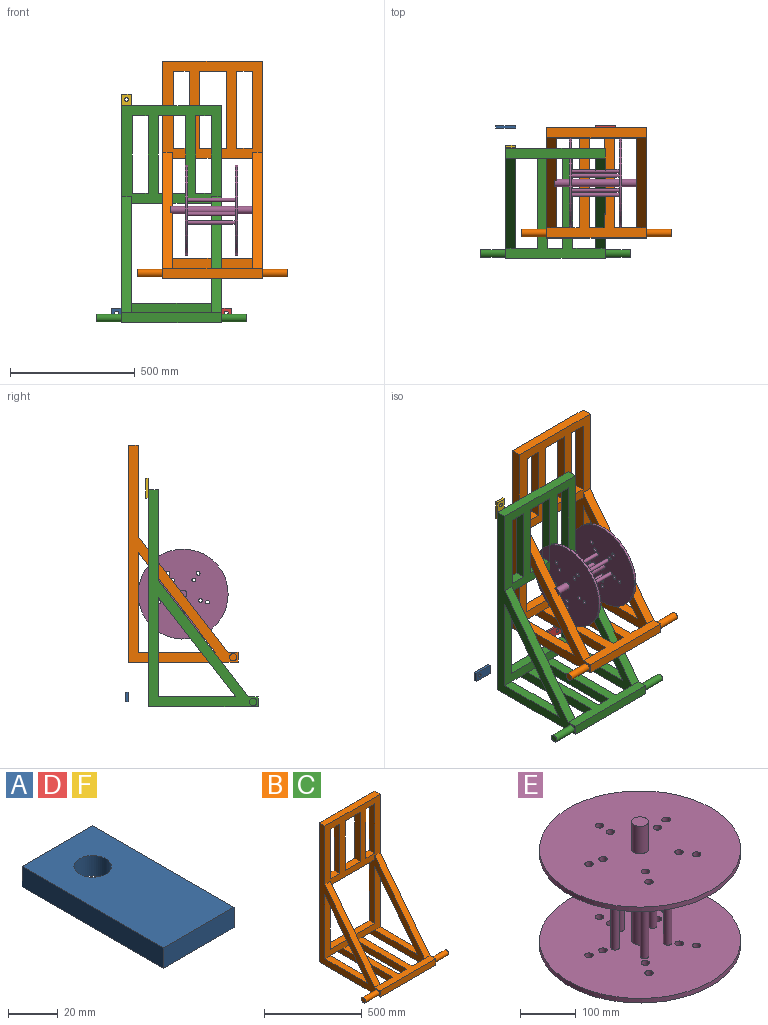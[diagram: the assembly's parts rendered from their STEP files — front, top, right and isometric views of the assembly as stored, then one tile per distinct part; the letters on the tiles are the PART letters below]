
ASSEMBLY  parts=6 mates=3
PART A: 7 faces, bbox 40x80x10 mm
  f0: plane 40x10mm, normal (0,1,0), area 400mm2, adj f1,f4,f5,f6
  f1: plane 80x10mm, normal (-1,0,0), area 800mm2, adj f0,f2,f5,f6
  f2: plane 40x10mm, normal (0,-1,0), area 400mm2, adj f1,f4,f5,f6
  f3: cylinder r=7.5mm len=15mm, axis (0,0,-1), area 471.2mm2, adj f5,f6
  f4: plane 80x10mm, normal (1,0,0), area 800mm2, adj f0,f2,f5,f6
  f5: plane 80x40mm, normal (0,0,1), area 3023.3mm2, adj f0,f1,f2,f3,f4
  f6: plane 80x40mm, normal (0,0,-1), area 3023.3mm2, adj f0,f1,f2,f3,f4
PART B: 45 faces, bbox 600x440x870 mm
  f0: plane 400x390mm, normal (0,-1,0), area 80507.1mm2, adj f5,f6,f7,f8,f9,f10,f11,f12
  f1: plane 400x400mm, normal (0,0,1), area 44800mm2, adj f8,f19,f24,f28,f29,f30,f31,f34
  f2: plane 90x40mm, normal (0,0,-1), area 3600mm2, adj f17,f24,f25,f30
  f3: plane 60x40mm, normal (0,0,-1), area 2400mm2, adj f24,f25,f29,f31
  f4: plane 90x40mm, normal (0,0,-1), area 3600mm2, adj f22,f24,f25,f28
  f5: plane 310x40mm, normal (-1,0,0), area 12400mm2, adj f0,f6,f23,f25
  f6: plane 109.75x40mm, normal (0,0,1), area 4390mm2, adj f0,f5,f7,f25
  f7: plane 310x40mm, normal (1,0,0), area 12400mm2, adj f0,f6,f23,f25
  f8: plane 870x440mm, normal (1,0,0), area 71974.7mm2, adj f0,f1,f9,f24,f25,f26,f27,f38
  f9: plane 400x40mm, normal (0,0,1), area 16000mm2, adj f0,f8,f19,f25
  f10: plane 63.61x40mm, normal (0,0,1), area 2544.6mm2, adj f0,f11,f20,f25
  f11: plane 310x40mm, normal (1,0,0), area 12400mm2, adj f0,f10,f12,f25
  f12: plane 63.61x40mm, normal (0,0,-1), area 2544.6mm2, adj f0,f11,f20,f25
  f13: plane 63.61x40mm, normal (0,0,1), area 2544.6mm2, adj f0,f14,f21,f25
  f14: plane 310x40mm, normal (1,0,0), area 12400mm2, adj f0,f13,f15,f25
  f15: plane 63.61x40mm, normal (0,0,-1), area 2544.6mm2, adj f0,f14,f21,f25
  f16: plane 320x40mm, normal (0,0,1), area 12800mm2, adj f17,f22,f24,f25
  f17: plane 505.37x400mm, normal (1,0,0), area 53881.6mm2, adj f0,f2,f16,f18,f24,f25,f27,f32
  f18: plane 320x40mm, normal (0,0,-1), area 12800mm2, adj f0,f17,f22,f25
  f19: plane 870x440mm, normal (-1,0,0), area 71974.7mm2, adj f0,f1,f9,f24,f25,f27,f32,f33
  f20: plane 310x40mm, normal (-1,0,0), area 12400mm2, adj f0,f10,f12,f25
  f21: plane 310x40mm, normal (-1,0,0), area 12400mm2, adj f0,f13,f15,f25
  f22: plane 505.37x400mm, normal (-1,0,0), area 53881.6mm2, adj f0,f4,f16,f18,f24,f25,f26,f27
  f23: plane 109.75x40mm, normal (0,0,-1), area 4390mm2, adj f0,f5,f7,f25
  f24: plane 400x400mm, normal (0,-1,0), area 44800mm2, adj f1,f2,f3,f4,f8,f16,f17,f19
  f25: plane 870x400mm, normal (0,1,0), area 136937mm2, adj f2,f3,f4,f5,f6,f7,f8,f9
  f26: plane 309.43x40mm, normal (0,0,1), area 12377.1mm2, adj f8,f22,f24,f40
  f27: plane 440x400mm, normal (0,0,-1), area 80000mm2, adj f8,f17,f19,f22,f25,f28,f29,f30
  f28: plane 400x40mm, normal (1,0,0), area 16000mm2, adj f1,f4,f25,f27,f35
  f29: plane 400x40mm, normal (-1,0,0), area 16000mm2, adj f1,f3,f25,f27,f36
  f30: plane 400x40mm, normal (-1,0,0), area 16000mm2, adj f1,f2,f25,f27,f37
  f31: plane 400x40mm, normal (1,0,0), area 16000mm2, adj f1,f3,f25,f27,f36
  f32: plane 309.43x40mm, normal (0,0,1), area 12377.1mm2, adj f17,f19,f24,f33
  f33: plane 400x309.43mm, normal (0,0.79,-0.61), area 20228.5mm2, adj f17,f19,f24,f32
  f34: plane 465.37x360mm, normal (0,-0.79,0.61), area 23534.6mm2, adj f0,f1,f17,f19
  f35: plane 90x40mm, normal (0,1,0), area 3600mm2, adj f1,f22,f27,f28
  f36: plane 60x40mm, normal (0,1,0), area 2400mm2, adj f1,f27,f29,f31
  f37: plane 90x40mm, normal (0,1,0), area 3600mm2, adj f1,f17,f27,f30
  f38: plane 400x40mm, normal (0,-1,0), area 16000mm2, adj f1,f8,f19,f27
  f39: plane 465.37x360mm, normal (0,-0.79,0.61), area 23534.6mm2, adj f0,f1,f8,f22
  f40: plane 400x309.43mm, normal (0,0.79,-0.61), area 20228.5mm2, adj f8,f22,f24,f26
  f41: cylinder r=15mm len=100mm, axis (-1,0,0), area 9424.8mm2, adj f8,f42
  f42: plane 30x30mm, normal (1,0,0), area 706.9mm2, adj f41
  f43: cylinder r=15mm len=100mm, axis (1,0,0), area 9424.8mm2, adj f19,f44
  f44: plane 30x30mm, normal (-1,0,0), area 706.9mm2, adj f43
PART C: same geometry as B
PART D: same geometry as A
PART E: 36 faces, bbox 360x360x330 mm
  f0: cylinder r=180mm len=360mm, axis (0,0,-1), area 11309.7mm2, adj f1,f2
  f1: plane 360x360mm, normal (0,0,1), area 98430mm2, adj f0,f3,f4,f5,f6,f7,f8,f26
  f2: plane 360x360mm, normal (0,0,-1), area 99313.6mm2, adj f0,f12,f26,f27,f28,f29,f30,f31
  f3: cylinder r=15mm len=190mm, axis (0,0,-1), area 17907.1mm2, adj f1,f11
  f4: cylinder r=7.5mm len=190mm, axis (0,0,-1), area 8953.5mm2, adj f1,f11
  f5: cylinder r=7.5mm len=190mm, axis (0,0,-1), area 8953.5mm2, adj f1,f11
  f6: cylinder r=7.5mm len=190mm, axis (0,0,-1), area 8953.5mm2, adj f1,f11
  f7: cylinder r=7.5mm len=190mm, axis (0,0,-1), area 8953.5mm2, adj f1,f11
  f8: cylinder r=7.5mm len=190mm, axis (0,0,-1), area 8953.5mm2, adj f1,f11
  f9: cylinder r=180mm len=360mm, axis (0,0,-1), area 11309.7mm2, adj f10,f11
  f10: plane 360x360mm, normal (0,0,1), area 99313.6mm2, adj f9,f14,f16,f17,f18,f19,f20,f21
  f11: plane 360x360mm, normal (0,0,-1), area 98430mm2, adj f3,f4,f5,f6,f7,f8,f9,f16
  f12: cylinder r=15mm len=60mm, axis (0,0,1), area 5654.9mm2, adj f2,f13
  f13: plane 30x30mm, normal (0,0,-1), area 706.9mm2, adj f12
  f14: cylinder r=15mm len=60mm, axis (0,0,-1), area 5654.9mm2, adj f10,f15
  f15: plane 30x30mm, normal (0,0,1), area 706.9mm2, adj f14
  f16: cylinder r=7.5mm len=15mm, axis (0,0,-1), area 471.2mm2, adj f10,f11
  f17: cylinder r=7.5mm len=15mm, axis (0,0,-1), area 471.2mm2, adj f10,f11
  f18: cylinder r=7.5mm len=15mm, axis (0,0,-1), area 471.2mm2, adj f10,f11
  f19: cylinder r=7.5mm len=15mm, axis (0,0,-1), area 471.2mm2, adj f10,f11
  f20: cylinder r=7.5mm len=15mm, axis (0,0,-1), area 471.2mm2, adj f10,f11
  f21: cylinder r=7.5mm len=15mm, axis (0,0,-1), area 471.2mm2, adj f10,f11
  f22: cylinder r=7.5mm len=15mm, axis (0,0,-1), area 471.2mm2, adj f10,f11
  f23: cylinder r=7.5mm len=15mm, axis (0,0,-1), area 471.2mm2, adj f10,f11
  f24: cylinder r=7.5mm len=15mm, axis (0,0,-1), area 471.2mm2, adj f10,f11
  f25: cylinder r=7.5mm len=15mm, axis (0,0,-1), area 471.2mm2, adj f10,f11
  f26: cylinder r=7.5mm len=15mm, axis (0,0,-1), area 471.2mm2, adj f1,f2
  f27: cylinder r=7.5mm len=15mm, axis (0,0,-1), area 471.2mm2, adj f1,f2
  f28: cylinder r=7.5mm len=15mm, axis (0,0,-1), area 471.2mm2, adj f1,f2
  f29: cylinder r=7.5mm len=15mm, axis (0,0,-1), area 471.2mm2, adj f1,f2
  f30: cylinder r=7.5mm len=15mm, axis (0,0,-1), area 471.2mm2, adj f1,f2
  f31: cylinder r=7.5mm len=15mm, axis (0,0,-1), area 471.2mm2, adj f1,f2
  f32: cylinder r=7.5mm len=15mm, axis (0,0,-1), area 471.2mm2, adj f1,f2
  f33: cylinder r=7.5mm len=15mm, axis (0,0,-1), area 471.2mm2, adj f1,f2
  f34: cylinder r=7.5mm len=15mm, axis (0,0,-1), area 471.2mm2, adj f1,f2
  f35: cylinder r=7.5mm len=15mm, axis (0,0,-1), area 471.2mm2, adj f1,f2
PART F: same geometry as A
PLACE A rot(axis=(-0.58,0.58,0.58),120deg) t=(-227.2,31.63,-720.68)mm
PLACE B t=(-102.52,31.63,268.85)mm
PLACE C t=(-267.2,-49.25,89.32)mm
PLACE D rot(axis=(-0.58,-0.58,-0.58),120deg) t=(92.8,31.63,-760.68)mm
PLACE E rot(axis=(-0.58,0.58,-0.58),120deg) t=(-12.52,-188.37,-328.46)mm
PLACE F rot(axis=(0,-0.71,-0.71),180deg) t=(-227.54,-48.15,55.11)mm
MATE planar A.f6 <-> B.f25  axis (0,-1,0) through (-227.2,31.63,-740.68)mm
MATE revolute E.f0 <-> B.f22  axis (1,0,0) through (257.48,-188.37,-328.46)mm
MATE planar D.f6 <-> B.f25  axis (0,-1,0) through (92.8,31.63,-740.68)mm
